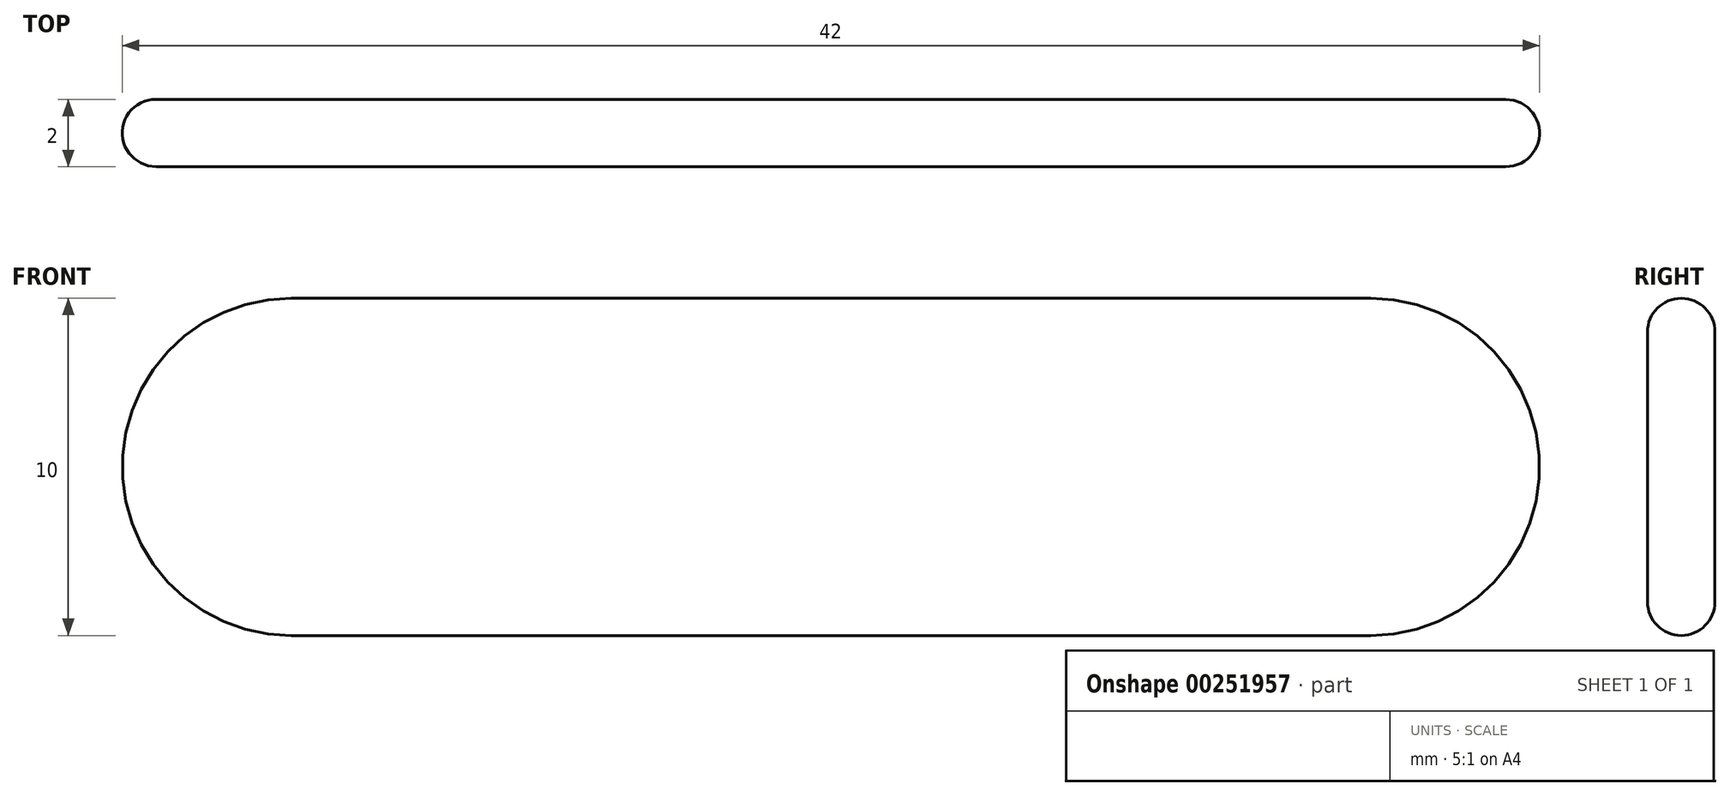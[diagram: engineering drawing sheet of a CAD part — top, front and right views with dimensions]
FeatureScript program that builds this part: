
annotation { "Feature Type Name" : "Feature", "Feature Type Description" : "" }
export const myFeature = defineFeature(function(context is Context, id is Id, definition is map)
    precondition{}
    {
        {
            var Q0;
            Q0=qCreatedBy(makeId("Front.planeOp"),FACE);
            var sketch = newSketch(context, id + "F0", { "sketchPlane" : qUnion([Q0])});
            skLineSegment(sketch, "E0.bottom", {"start": v(-16, 5) * mm, "end": v(16, 5) * mm});
            skLineSegment(sketch, "E0.top", {"start": v(-16, -5) * mm, "end": v(16, -5) * mm});
            skLineSegment(sketch, "E0.left", {"start": v(-21, 0) * mm, "end": v(-21, 0) * mm});
            skLineSegment(sketch, "E0.right", {"start": v(21, 0) * mm, "end": v(21, 0) * mm});
            skPoint(sketch, "E0.middle", {"position": v(0, 0) * mm});
            skPoint(sketch, "E1.visualSharp", {"position": v(-21, 5) * mm});
            skArc(sketch, "E1.filletArc", {"start": v(-16, 5) * mm, "mid": v(-19.54, 3.54) * mm, "end": v(-21, 0) * mm});
            skPoint(sketch, "E2.visualSharp", {"position": v(-21, -5) * mm});
            skArc(sketch, "E2.filletArc", {"start": v(-21, 0) * mm, "mid": v(-19.54, -3.54) * mm, "end": v(-16, -5) * mm});
            skPoint(sketch, "E3.visualSharp", {"position": v(21, 5) * mm});
            skArc(sketch, "E3.filletArc", {"start": v(21, 0) * mm, "mid": v(19.54, 3.54) * mm, "end": v(16, 5) * mm});
            skPoint(sketch, "E4.visualSharp", {"position": v(21, -5) * mm});
            skArc(sketch, "E4.filletArc", {"start": v(16, -5) * mm, "mid": v(19.54, -3.54) * mm, "end": v(21, 0) * mm});
            skSolve(sketch);
        }
        {
            var Q0;
            Q0=qSketchRegion(id+"F0",true);
            extrude(context, id + "F1", {"entities" : qUnion([Q0]), "depth" : 2 * mm});
        }
        {
            var Q0;
            Q0=makeQuery(id+"F1.opExtrude","CAP_FACE",FACE,{"disambiguationData":[OSD([sQuery(id+"F0.wireOp",EDGE,"E0.bottom"),sQuery(id+"F0.wireOp",EDGE,"E0.top"),sQuery(id+"F0.wireOp",EDGE,"E1.filletArc"),sQuery(id+"F0.wireOp",EDGE,"E2.filletArc"),sQuery(id+"F0.wireOp",EDGE,"E3.filletArc"),sQuery(id+"F0.wireOp",EDGE,"E4.filletArc")])],"isStart":false});
            var Q1;
            Q1=makeQuery(id+"F1.opExtrude","CAP_FACE",FACE,{"disambiguationData":[OSD([sQuery(id+"F0.wireOp",EDGE,"E0.bottom"),sQuery(id+"F0.wireOp",EDGE,"E0.top"),sQuery(id+"F0.wireOp",EDGE,"E1.filletArc"),sQuery(id+"F0.wireOp",EDGE,"E2.filletArc"),sQuery(id+"F0.wireOp",EDGE,"E3.filletArc"),sQuery(id+"F0.wireOp",EDGE,"E4.filletArc")])],"isStart":true});
            fillet(context, id + "F2", {"entities" : qUnion([Q0, Q1]), "radius" : 1 * mm, "tangentPropagation" : true, "allowEdgeOverflow" : false});
        }
    });
